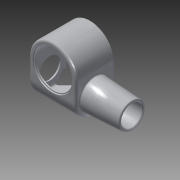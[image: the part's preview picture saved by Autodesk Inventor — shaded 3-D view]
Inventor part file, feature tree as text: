
AUTODESK INVENTOR PART (.ipt)
format: ipt  version: 2014 (Build 180170000, 170)  size: 304,640 bytes
history: native  units: mm (DEFAULTED — no unit token found)
features: extrude x9, sketch x9, fillet x7, chamfer x3, shell x1
ambient origin geometry x8: Origin, YZ Plane, XZ Plane, XY Plane, X Axis, Y Axis, Z Axis, Center Point
bodies: Solid1 (feature_tree)
feature tree (29):
  extrude  "Extrusion1"  Depth=2.286mm TaperAngle=0.0deg
  fillet  "Fillet7"  Radius=0.762mm
  shell  "Shell1"  Thickness=0.762mm
  extrude  "Extrusion2"  Depth=2.38125mm
  fillet  "Fillet1"  Radius=2.286mm
  fillet  "Fillet2"  Radius=2.286mm
  fillet  "Fillet3"  Radius=0.79375mm
  extrude  "Extrusion3"  Depth=0.79375mm TaperAngle=0.0deg
  fillet  "Fillet8"  Radius=0.396875mm
  extrude  "Extrusion5"  Depth=12.7mm
  extrude  "Extrusion6"  Depth=0.381mm
  extrude  "Extrusion7"  Depth=7.14375mm
  extrude  "Extrusion8"  Depth=0.254mm
  fillet  "Fillet5"  Radius=7.9375mm
  fillet  "Fillet6"  Radius=0.396875mm
  extrude  "Extrusion9"  Depth=0.79375mm
  chamfer  "Chamfer2"  Distance=0.396875mm
  extrude  "Extrusion10"  Depth=0.127mm
  chamfer  "Chamfer5"  Angle=45.0deg  [1 undecoded]
  chamfer  "Chamfer6"  Distance=0.127mm Angle=45.0deg
  sketch  "Sketch1"  dims[d0=12.7mm d1=0.0mm d4=2.286mm d5=0.0mm d6=0.762mm d7=0.762mm]
  sketch  "Sketch2"  dims[d8=0.762mm d10=2.38125mm d11=2.286mm d12=2.286mm d13=0.0mm d19=0.79375mm d20=0.0mm]
  sketch  "Sketch3"  dims[d21=7.9375mm d23=0.79375mm d24=0.0mm d25=0.396875mm]
  sketch  "Sketch5"  dims[d26=0.396875mm d27=0.0mm d28=12.7mm]
  sketch  "Sketch6"  dims[d32=12.7mm d33=-0.523599mm d34=0.381mm]
  sketch  "Sketch7"  dims[d35=0.381mm d36=7.14375mm]
  sketch  "Sketch8"  dims[d37=12.7mm d38=0.0mm d41=0.254mm d42=0.254mm d43=7.9375mm d44=0.396875mm d45=0.0mm]
  sketch  "Sketch9"  dims[d50=6.35mm d51=0.79375mm]
  sketch  "Sketch10"  dims[d52=0.762mm d53=0.396875mm d54=0.127mm d55=0.127mm d56=45.0deg d58=45.0deg d59=0.127mm d60=3.175mm d61=45.0deg]
note: 1 required parameter value undecoded (feature->parameter linkage not recoverable at this tier; creation-order binding heuristic only, values carry confidence <= 0.55)
